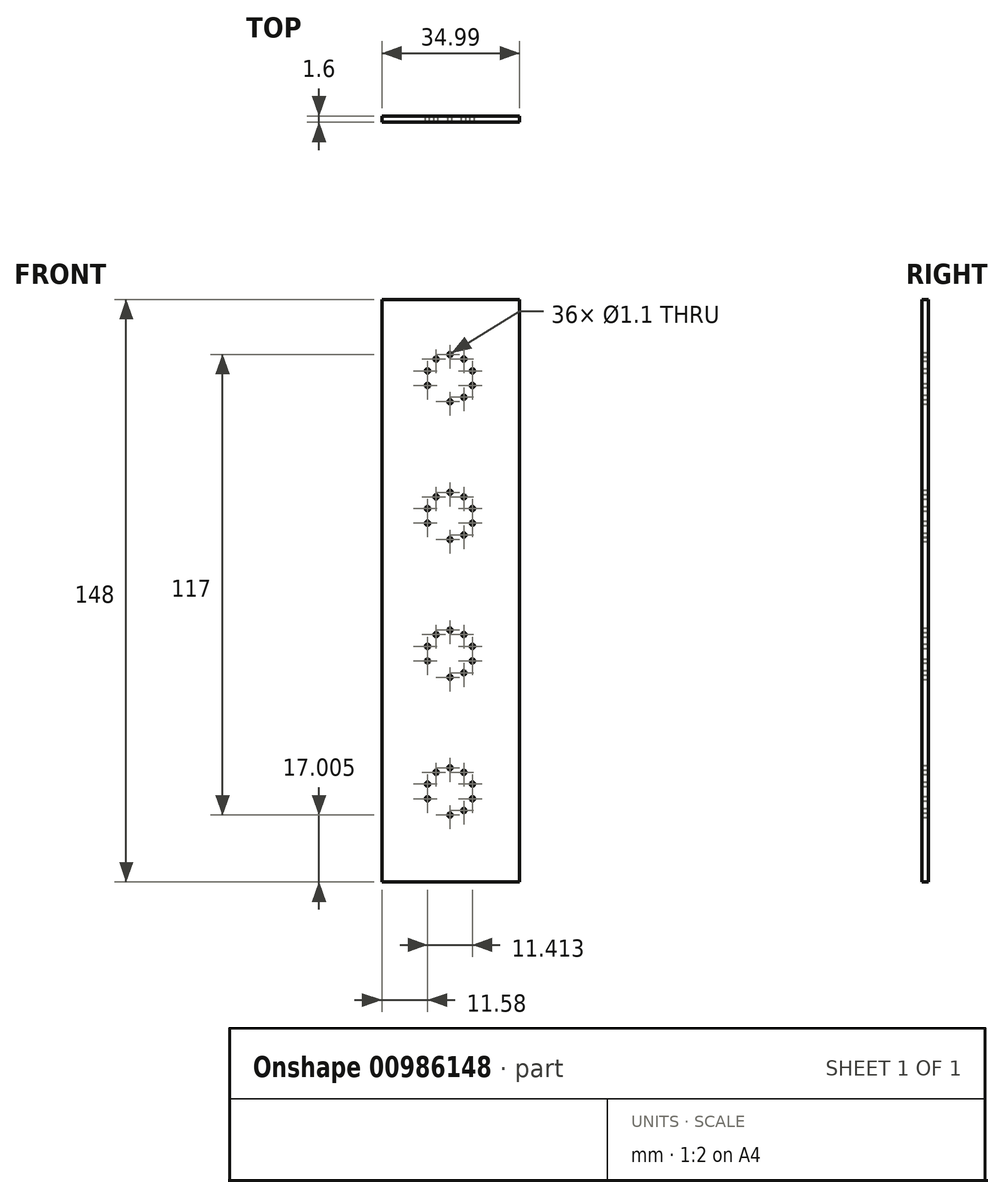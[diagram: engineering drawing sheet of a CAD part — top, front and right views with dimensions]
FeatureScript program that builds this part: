
annotation { "Feature Type Name" : "Feature", "Feature Type Description" : "" }
export const myFeature = defineFeature(function(context is Context, id is Id, definition is map)
    precondition{}
    {
        {
            var Q0;
            Q0=qCreatedBy(makeId("Front.planeOp"),FACE);
            var sketch = newSketch(context, id + "F0", { "sketchPlane" : qUnion([Q0])});
            skLineSegment(sketch, "E0.0.0", {"start": v(-17.66, -75.84) * mm, "end": v(17.33, -75.84) * mm});
            skLineSegment(sketch, "E0.0.1", {"start": v(17.33, -75.84) * mm, "end": v(17.33, 72.16) * mm});
            skLineSegment(sketch, "E0.0.2", {"start": v(17.33, 72.16) * mm, "end": v(-17.66, 72.16) * mm});
            skLineSegment(sketch, "E0.0.3", {"start": v(-17.66, 72.16) * mm, "end": v(-17.66, -75.84) * mm});
            skCircle(sketch, "E1.0", {"center": v(-6.08, 50.31) * mm, "radius": 0.55 * mm});
            skCircle(sketch, "E2.0", {"center": v(-6.08, 54.02) * mm, "radius": 0.55 * mm});
            skCircle(sketch, "E3.0", {"center": v(-3.9, 57.02) * mm, "radius": 0.55 * mm});
            skCircle(sketch, "E4.0", {"center": v(-0.37, 58.16) * mm, "radius": 0.55 * mm});
            skCircle(sketch, "E5.0", {"center": v(3.15, 57.02) * mm, "radius": 0.55 * mm});
            skCircle(sketch, "E6.0", {"center": v(5.33, 54.02) * mm, "radius": 0.55 * mm});
            skCircle(sketch, "E7.0", {"center": v(5.33, 50.31) * mm, "radius": 0.55 * mm});
            skCircle(sketch, "E8.0", {"center": v(3.15, 47.31) * mm, "radius": 0.55 * mm});
            skCircle(sketch, "E9.0", {"center": v(-0.37, 46.16) * mm, "radius": 0.55 * mm});
            skCircle(sketch, "E10.0", {"center": v(-6.08, 15.31) * mm, "radius": 0.55 * mm});
            skCircle(sketch, "E11.0", {"center": v(-6.08, 19.02) * mm, "radius": 0.55 * mm});
            skCircle(sketch, "E12.0", {"center": v(-3.9, 22.02) * mm, "radius": 0.55 * mm});
            skCircle(sketch, "E13.0", {"center": v(-0.37, 23.16) * mm, "radius": 0.55 * mm});
            skCircle(sketch, "E14.0", {"center": v(3.15, 22.02) * mm, "radius": 0.55 * mm});
            skCircle(sketch, "E15.0", {"center": v(5.33, 19.02) * mm, "radius": 0.55 * mm});
            skCircle(sketch, "E16.0", {"center": v(5.33, 15.31) * mm, "radius": 0.55 * mm});
            skCircle(sketch, "E17.0", {"center": v(3.15, 12.31) * mm, "radius": 0.55 * mm});
            skCircle(sketch, "E18.0", {"center": v(-0.37, 11.16) * mm, "radius": 0.55 * mm});
            skCircle(sketch, "E19.0", {"center": v(-0.37, -23.84) * mm, "radius": 0.55 * mm});
            skCircle(sketch, "E20.0", {"center": v(-6.08, -19.69) * mm, "radius": 0.55 * mm});
            skCircle(sketch, "E21.0", {"center": v(-6.08, -15.98) * mm, "radius": 0.55 * mm});
            skCircle(sketch, "E22.0", {"center": v(-3.9, -12.98) * mm, "radius": 0.55 * mm});
            skCircle(sketch, "E23.0", {"center": v(-0.37, -11.84) * mm, "radius": 0.55 * mm});
            skCircle(sketch, "E24.0", {"center": v(3.15, -12.98) * mm, "radius": 0.55 * mm});
            skCircle(sketch, "E25.0", {"center": v(5.33, -15.98) * mm, "radius": 0.55 * mm});
            skCircle(sketch, "E26.0", {"center": v(5.33, -19.69) * mm, "radius": 0.55 * mm});
            skCircle(sketch, "E27.0", {"center": v(3.15, -22.69) * mm, "radius": 0.55 * mm});
            skCircle(sketch, "E28.0", {"center": v(-6.08, -54.69) * mm, "radius": 0.55 * mm});
            skCircle(sketch, "E29.0", {"center": v(-6.08, -50.98) * mm, "radius": 0.55 * mm});
            skCircle(sketch, "E30.0", {"center": v(-3.9, -47.98) * mm, "radius": 0.55 * mm});
            skCircle(sketch, "E31.0", {"center": v(-0.37, -46.84) * mm, "radius": 0.55 * mm});
            skCircle(sketch, "E32.0", {"center": v(3.15, -47.98) * mm, "radius": 0.55 * mm});
            skCircle(sketch, "E33.0", {"center": v(5.33, -50.98) * mm, "radius": 0.55 * mm});
            skCircle(sketch, "E34.0", {"center": v(5.33, -54.69) * mm, "radius": 0.55 * mm});
            skCircle(sketch, "E35.0", {"center": v(3.15, -57.69) * mm, "radius": 0.55 * mm});
            skCircle(sketch, "E36.0", {"center": v(-0.37, -58.84) * mm, "radius": 0.55 * mm});
            skSolve(sketch);
        }
        {
            var Q0;
            Q0=makeQuery(id+"F0.imprint","IMPRINT",FACE,{"disambiguationData":[TD([[makeQuery(id+"F0.imprint","IMPRINT",EDGE,{"derivedFrom":sQuery(id+"F0.wireOp",EDGE,"E0.0.0")}),1.0]])]});
            extrude(context, id + "F1", {"entities" : qUnion([Q0]), "depth" : 1.6 * mm, "offsetDistance" : 25 * mm});
        }
    });
